# Revit family: FU_Inspec_Archal_1-7-LB
name_source: partatom
category: Furniture
units: mm (PartAtom-declared; Revit-internal decimal feet)

## family parameters
Always vertical = Yes
Cut with Voids When Loaded = No
OmniClass Number = 23.40.20.00
OmniClass Title = General Furniture and Specialties
Room Calculation Point = No
Shared = No
Work Plane-Based = No

## types (2) — shared parameters
Armrest Material = Metal - Chrome - Polished
Assembly Code = E2020
Castor Material = Plastic - Black
Frame Material = Metal - Chrome - Polished
Keynote = 46.B
Manufacturer = Inspec
Not Quilted = No
Quilted = Yes
Solid Seat = No
URL = https://inspecfurniture.com
zero-valued in all types: Default Elevation

## per-type parameters (varying)
| type | Description | Not Upholstered | Seat Material | Upholstered |
| archal 2.7 lb | 360° swivel low back armchair on a powder coated or chromium plated steel base, casters in chrome or black, upholstery with quilting detail. | No | Fabric Grey | Yes |
| archal 1.7 lb | 360° swivel low back chair on a powder coated or chromium plated steel base, casters in chrome or black, upholstery with quilting detail. | Yes | Leather - Rustical - Dark brown | No |

note: column(s) folded — value = type name in every type: Model

## geometry (parser evidence)
native form markers: Blend x13, Sweep x2
no freeform markers — native parametric forms only
